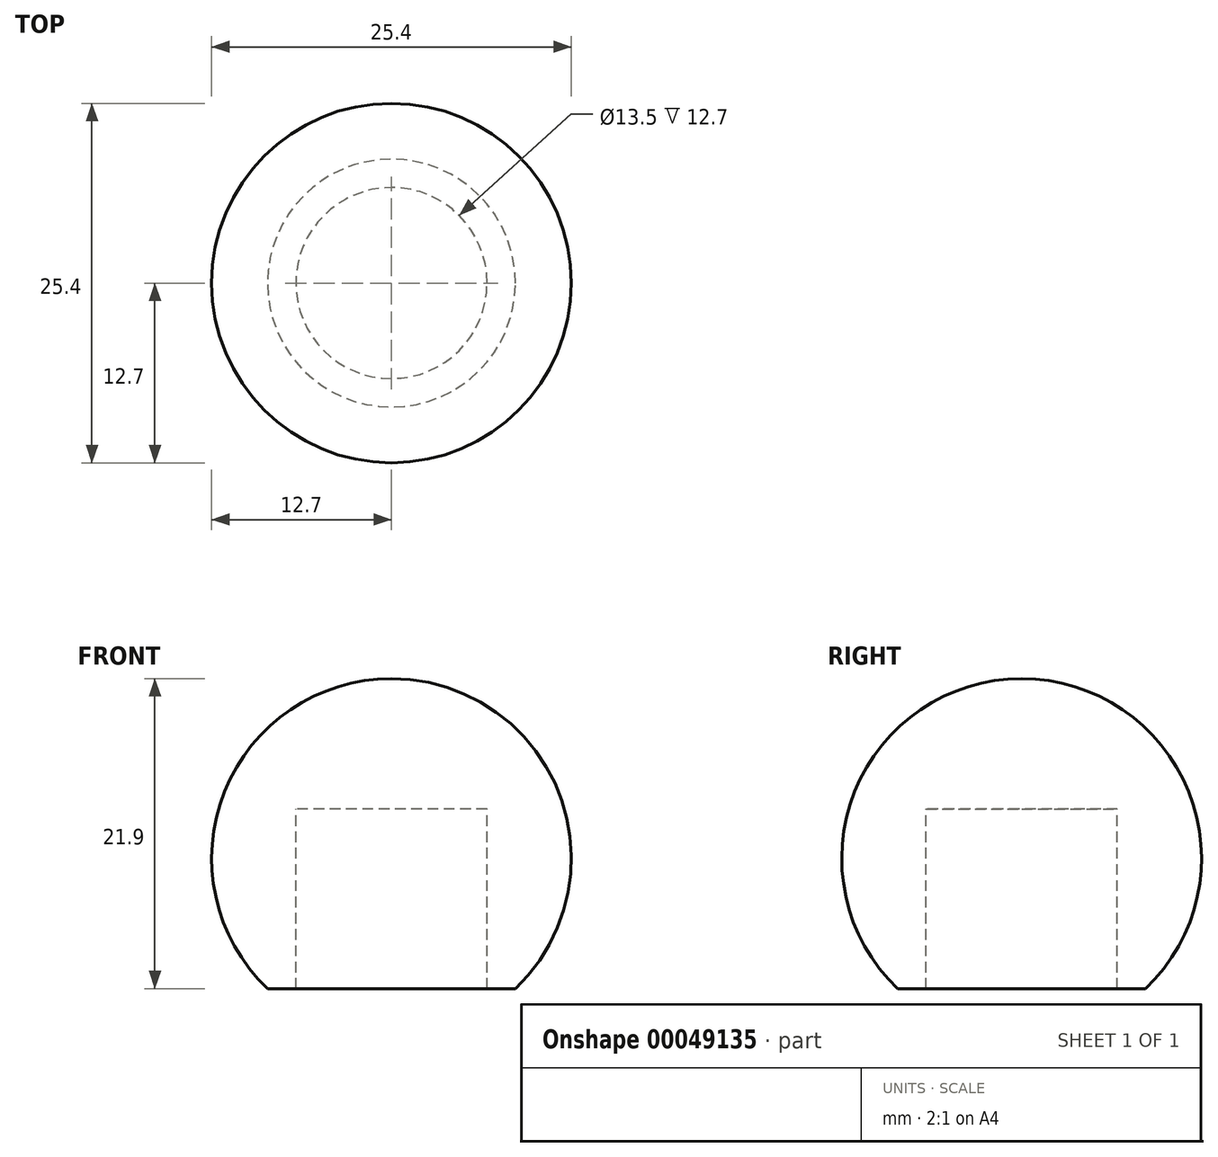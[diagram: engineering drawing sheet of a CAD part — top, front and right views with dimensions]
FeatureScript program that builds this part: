
annotation { "Feature Type Name" : "Feature", "Feature Type Description" : "" }
export const myFeature = defineFeature(function(context is Context, id is Id, definition is map)
    precondition{}
    {
        {
            var Q0;
            Q0=qCreatedBy(makeId("Front.planeOp"),FACE);
            var sketch = newSketch(context, id + "F0", { "sketchPlane" : qUnion([Q0])});
            skArc(sketch, "E0", {"start": v(0, 12.7) * mm, "mid": v(11.8, 4.71) * mm, "end": v(8.75, -9.2) * mm});
            skLineSegment(sketch, "E1", {"start": v(0, -21.69) * mm, "end": v(0, 22.34) * mm, "construction": true});
            skLineSegment(sketch, "E2", {"start": v(0, 3.5) * mm, "end": v(6.75, 3.5) * mm});
            skLineSegment(sketch, "E3", {"start": v(6.75, 3.5) * mm, "end": v(6.75, -9.2) * mm});
            skLineSegment(sketch, "E4", {"start": v(6.75, -9.2) * mm, "end": v(8.75, -9.2) * mm});
            skLineSegment(sketch, "E5", {"start": v(0, 12.7) * mm, "end": v(0, 3.5) * mm});
            skSolve(sketch);
        }
        {
            var Q0;
            Q0=qCreatedBy(makeId("Front.planeOp"),FACE);
            var sketch = newSketch(context, id + "F1", { "sketchPlane" : qUnion([Q0])});
            skLineSegment(sketch, "E6", {"start": v(0, 15.78) * mm, "end": v(0, -17.02) * mm, "construction": true});
            skSolve(sketch);
        }
        {
            var Q0;
            Q0 = qSketchRegion(id + "F0", true);
            var Q1;
            Q1=sQuery(id+"F1.wireOp",EDGE,"E6");
            revolve(context, id + "F2", {"entities" : qUnion([Q0]), "axis" : qUnion([Q1]), "revolveType" : RevolveType.FULL});
        }
    });
